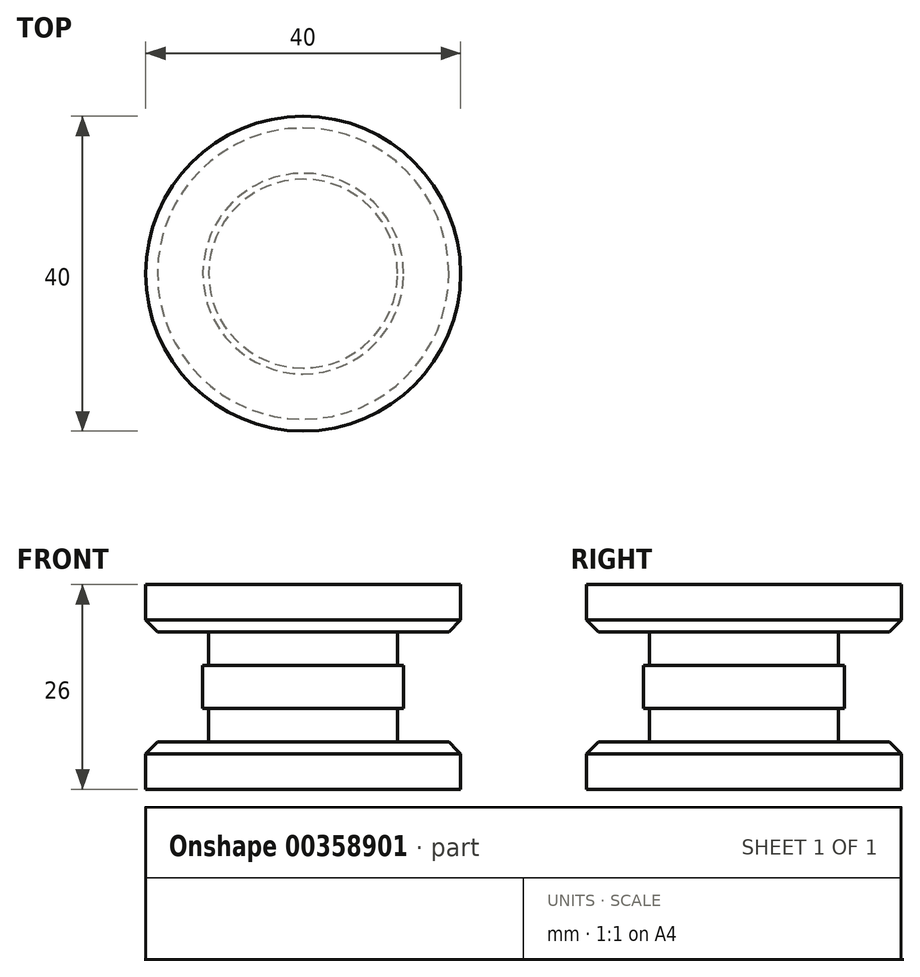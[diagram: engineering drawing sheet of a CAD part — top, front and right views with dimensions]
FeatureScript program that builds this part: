
annotation { "Feature Type Name" : "Feature", "Feature Type Description" : "" }
export const myFeature = defineFeature(function(context is Context, id is Id, definition is map)
    precondition{}
    {
        {
            var Q0;
            Q0=qCreatedBy(makeId("Top.planeOp"),FACE);
            var sketch = newSketch(context, id + "F0", { "sketchPlane" : qUnion([Q0])});
            skCircle(sketch, "E0", {"center": v(0, 0) * mm, "radius": 20 * mm});
            skSolve(sketch);
        }
        {
            var Q0;
            Q0 = qSketchRegion(id + "F0", true);
            extrude(context, id + "F1", {"entities" : qUnion([Q0]), "depth" : 6 * mm});
        }
        {
            var Q0;
            Q0=makeQuery(id+"F1.opExtrude","CAP_EDGE",EDGE,{"disambiguationData":[OSD([sQuery(id+"F0.wireOp",EDGE,"E0")])],"isStart":false});
            chamfer(context, id + "F2", {"entities" : qUnion([Q0]), "width" : 1.5 * mm, "tangentPropagation" : true});
        }
        {
            var Q0;
            Q0=qCreatedBy(makeId("Top.planeOp"),FACE);
            cPlane(context, id + "F3", {"entities" : qUnion([Q0]), "cplaneType" : CPlaneType.OFFSET, "offset" : 6 * mm, "width" : 150 * mm, "height" : 150 * mm});
        }
        {
            var Q0;
            Q0=qCreatedBy(id+"F3.planeOp",FACE);
            var sketch = newSketch(context, id + "F4", { "sketchPlane" : qUnion([Q0])});
            skCircle(sketch, "E1", {"center": v(0, 0) * mm, "radius": 12 * mm});
            skSolve(sketch);
        }
        {
            var Q0;
            Q0 = qSketchRegion(id + "F4", true);
            extrude(context, id + "F5", {"entities" : qUnion([Q0]), "operationType" : NewBodyOperationType.ADD, "depth" : 4.25 * mm});
        }
        {
            var Q0;
            Q0=qCreatedBy(makeId("Top.planeOp"),FACE);
            cPlane(context, id + "F6", {"entities" : qUnion([Q0]), "cplaneType" : CPlaneType.OFFSET, "offset" : 10.25 * mm, "width" : 150 * mm, "height" : 150 * mm});
        }
        {
            var Q0;
            Q0=qCreatedBy(id+"F6.planeOp",FACE);
            var sketch = newSketch(context, id + "F7", { "sketchPlane" : qUnion([Q0])});
            skCircle(sketch, "E2", {"center": v(0, 0) * mm, "radius": 12.75 * mm});
            skSolve(sketch);
        }
        {
            var Q0;
            Q0 = qSketchRegion(id + "F7", true);
            extrude(context, id + "F8", {"entities" : qUnion([Q0]), "operationType" : NewBodyOperationType.ADD, "depth" : 5.5 * mm});
        }
        {
            var Q0;
            Q0=qCreatedBy(makeId("Top.planeOp"),FACE);
            cPlane(context, id + "F9", {"entities" : qUnion([Q0]), "cplaneType" : CPlaneType.OFFSET, "offset" : 15.75 * mm, "width" : 150 * mm, "height" : 150 * mm});
        }
        {
            var Q0;
            Q0=qCreatedBy(id+"F9.planeOp",FACE);
            var sketch = newSketch(context, id + "F10", { "sketchPlane" : qUnion([Q0])});
            skCircle(sketch, "E3", {"center": v(0, 0) * mm, "radius": 12 * mm});
            skSolve(sketch);
        }
        {
            var Q0;
            Q0 = qSketchRegion(id + "F10", true);
            extrude(context, id + "F11", {"entities" : qUnion([Q0]), "operationType" : NewBodyOperationType.ADD, "depth" : 4.25 * mm});
        }
        {
            var Q0;
            Q0=qCreatedBy(makeId("Top.planeOp"),FACE);
            cPlane(context, id + "F12", {"entities" : qUnion([Q0]), "cplaneType" : CPlaneType.OFFSET, "offset" : 20 * mm, "width" : 150 * mm, "height" : 150 * mm});
        }
        {
            var Q0;
            Q0=qCreatedBy(id+"F12.planeOp",FACE);
            var sketch = newSketch(context, id + "F13", { "sketchPlane" : qUnion([Q0])});
            skCircle(sketch, "E4", {"center": v(0, 0) * mm, "radius": 20 * mm});
            skSolve(sketch);
        }
        {
            var Q0;
            Q0 = qSketchRegion(id + "F13", true);
            extrude(context, id + "F14", {"entities" : qUnion([Q0]), "operationType" : NewBodyOperationType.ADD, "depth" : 6 * mm});
        }
        {
            var Q0;
            Q0=makeQuery(id+"F14.opExtrude","CAP_EDGE",EDGE,{"disambiguationData":[OSD([sQuery(id+"F13.wireOp",EDGE,"E4")])],"isStart":true});
            chamfer(context, id + "F15", {"entities" : qUnion([Q0]), "width" : 1.5 * mm, "tangentPropagation" : true});
        }
    });
